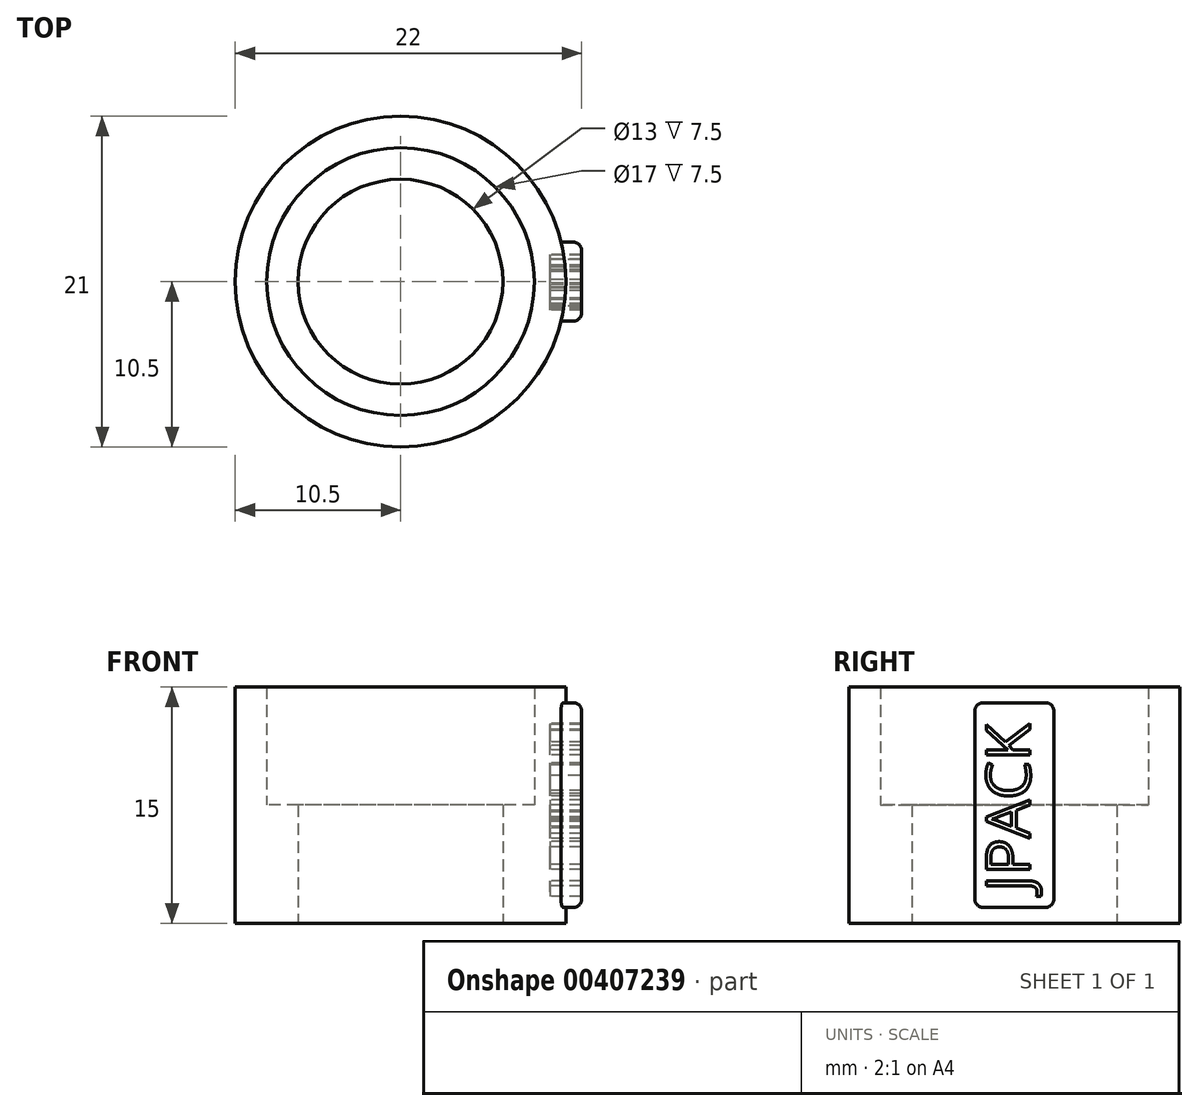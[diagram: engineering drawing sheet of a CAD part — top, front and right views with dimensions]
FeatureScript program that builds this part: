
annotation { "Feature Type Name" : "Feature", "Feature Type Description" : "" }
export const myFeature = defineFeature(function(context is Context, id is Id, definition is map)
    precondition{}
    {
        {
            var Q0;
            Q0=qCreatedBy(makeId("Top.planeOp"),FACE);
            var sketch = newSketch(context, id + "F0", { "sketchPlane" : qUnion([Q0])});
            skLineSegment(sketch, "E0", {"start": v(0, 0) * mm, "end": v(10.5, 0) * mm, "construction": true});
            skLineSegment(sketch, "E1", {"start": v(0, 0) * mm, "end": v(6.5, 0) * mm, "construction": true});
            skCircle(sketch, "E2", {"center": v(0, 0) * mm, "radius": 10.5 * mm});
            skCircle(sketch, "E3", {"center": v(0, 0) * mm, "radius": 6.5 * mm});
            skSolve(sketch);
        }
        {
            var Q0;
            Q0=makeQuery(id+"F0.imprint","IMPRINT",FACE,{"disambiguationData":[TD([[makeQuery(id+"F0.imprint","IMPRINT",EDGE,{"derivedFrom":sQuery(id+"F0.wireOp",EDGE,"E2")}),1.0]])]});
            cPlane(context, id + "F1", {"entities" : qUnion([Q0]), "cplaneType" : CPlaneType.OFFSET, "offset" : 5.5 * mm, "width" : 150 * mm, "height" : 150 * mm});
        }
        {
            var Q0;
            Q0=qCreatedBy(id+"F1.planeOp",FACE);
            cPlane(context, id + "F2", {"entities" : qUnion([Q0]), "cplaneType" : CPlaneType.OFFSET, "offset" : 2 * mm, "width" : 150 * mm, "height" : 150 * mm});
        }
        {
            var Q0;
            Q0=qCreatedBy(id+"F1.planeOp",FACE);
            var sketch = newSketch(context, id + "F3", { "sketchPlane" : qUnion([Q0])});
            skLineSegment(sketch, "E4", {"start": v(0, 0) * mm, "end": v(10.5, 0) * mm, "construction": true});
            skCircle(sketch, "E5", {"center": v(0, 0) * mm, "radius": 10.5 * mm});
            skSolve(sketch);
        }
        {
            var Q0;
            Q0 = qSketchRegion(id + "F3", true);
            extrude(context, id + "F4", {"entities" : qUnion([Q0]), "depth" : 2 * mm});
        }
        {
            var Q0;
            Q0 = qSketchRegion(id + "F0", true);
            extrude(context, id + "F5", {"entities" : qUnion([Q0]), "operationType" : NewBodyOperationType.ADD, "depth" : 5.5 * mm});
        }
        {
            var Q0;
            Q0=qCreatedBy(id+"F2.planeOp",FACE);
            var sketch = newSketch(context, id + "F6", { "sketchPlane" : qUnion([Q0])});
            skLineSegment(sketch, "E6", {"start": v(0, 0) * mm, "end": v(8.5, 0) * mm, "construction": true});
            skLineSegment(sketch, "E7", {"start": v(0, 0) * mm, "end": v(10.5, 0) * mm, "construction": true});
            skCircle(sketch, "E8", {"center": v(0, 0) * mm, "radius": 8.5 * mm});
            skCircle(sketch, "E9", {"center": v(0, 0) * mm, "radius": 10.5 * mm});
            skSolve(sketch);
        }
        {
            var Q0;
            Q0 = qSketchRegion(id + "F6", true);
            extrude(context, id + "F7", {"entities" : qUnion([Q0]), "operationType" : NewBodyOperationType.ADD, "depth" : 7.5 * mm});
        }
        {
            var Q0;
            Q0=qCreatedBy(makeId("Right.planeOp"),FACE);
            cPlane(context, id + "F8", {"entities" : qUnion([Q0]), "cplaneType" : CPlaneType.OFFSET, "offset" : 9.5 * mm, "width" : 150 * mm, "height" : 150 * mm});
        }
        {
            var Q0;
            Q0=qCreatedBy(id+"F8.planeOp",FACE);
            var sketch = newSketch(context, id + "F9", { "sketchPlane" : qUnion([Q0])});
            skLineSegment(sketch, "E10", {"start": v(0, 1) * mm, "end": v(0, 14) * mm, "construction": true});
            skLineSegment(sketch, "E11", {"start": v(0, 1) * mm, "end": v(0, 0) * mm, "construction": true});
            skLineSegment(sketch, "E12", {"start": v(0, 1) * mm, "end": v(2.5, 1) * mm});
            skLineSegment(sketch, "E13", {"start": v(2.5, 1) * mm, "end": v(2.5, 14) * mm});
            skLineSegment(sketch, "E14", {"start": v(2.5, 14) * mm, "end": v(0, 14) * mm});
            skLineSegment(sketch, "E15", {"start": v(0, 1) * mm, "end": v(-2.5, 1) * mm});
            skLineSegment(sketch, "E16", {"start": v(-2.5, 1) * mm, "end": v(-2.5, 14) * mm});
            skLineSegment(sketch, "E17", {"start": v(-2.5, 14) * mm, "end": v(0, 14) * mm});
            skSolve(sketch);
        }
        {
            var Q0;
            Q0 = qSketchRegion(id + "F9", true);
            extrude(context, id + "F10", {"entities" : qUnion([Q0]), "operationType" : NewBodyOperationType.ADD, "depth" : 2 * mm});
        }
        {
            var Q0;
            Q0=makeQuery(id+"F10.opExtrude","CAP_EDGE",EDGE,{"disambiguationData":[OSD([sQuery(id+"F9.wireOp",EDGE,"E14"),sQuery(id+"F9.wireOp",EDGE,"E17")])],"isStart":false});
            var Q1;
            Q1=makeQuery(id+"F10.opExtrude","CAP_EDGE",EDGE,{"disambiguationData":[OSD([sQuery(id+"F9.wireOp",EDGE,"E13")])],"isStart":false});
            var Q2;
            Q2=makeQuery(id+"F10.opExtrude","CAP_EDGE",EDGE,{"disambiguationData":[OSD([sQuery(id+"F9.wireOp",EDGE,"E12"),sQuery(id+"F9.wireOp",EDGE,"E15")])],"isStart":false});
            var Q3;
            Q3=makeQuery(id+"F10.opExtrude","CAP_EDGE",EDGE,{"disambiguationData":[OSD([sQuery(id+"F9.wireOp",EDGE,"E16")])],"isStart":false});
            var Q4;
            Q4=makeQuery(id+"F10.opExtrude","SWEPT_EDGE",EDGE,{"disambiguationData":[OSD([sQuery(id+"F9.wireOp",EDGE,"E13"),sQuery(id+"F9.wireOp",EDGE,"E14")])]});
            var Q5;
            Q5=makeQuery(id+"F10.opExtrude","SWEPT_EDGE",EDGE,{"disambiguationData":[OSD([sQuery(id+"F9.wireOp",EDGE,"E12"),sQuery(id+"F9.wireOp",EDGE,"E13")])]});
            var Q6;
            Q6=makeQuery(id+"F10.opExtrude","SWEPT_EDGE",EDGE,{"disambiguationData":[OSD([sQuery(id+"F9.wireOp",EDGE,"E16"),sQuery(id+"F9.wireOp",EDGE,"E17")])]});
            var Q7;
            Q7=makeQuery(id+"F10.opExtrude","SWEPT_EDGE",EDGE,{"disambiguationData":[OSD([sQuery(id+"F9.wireOp",EDGE,"E15"),sQuery(id+"F9.wireOp",EDGE,"E16")])]});
            fillet(context, id + "F11", {"entities" : qUnion([Q0, Q1, Q2, Q3, Q4, Q5, Q6, Q7]), "radius" : 0.5 * mm, "tangentPropagation" : true, "allowEdgeOverflow" : false});
        }
        {
            var Q0;
            Q0=qCreatedBy(id+"F8.planeOp",FACE);
            var sketch = newSketch(context, id + "F12", { "sketchPlane" : qUnion([Q0])});
            skLineSegment(sketch, "E18", {"start": v(0, 0) * mm, "end": v(0, 2) * mm, "construction": true});
            skLineSegment(sketch, "E19", {"start": v(0, 2) * mm, "end": v(-1.8, 2) * mm, "construction": true});
            skLineSegment(sketch, "E20", {"start": v(0, 2) * mm, "end": v(1, 2) * mm, "construction": true});
            skText(sketch, "E21", { "text": "JPACK", "fontName": "OpenSans-Regular.ttf"});
            const initialGuessF12  = {"E21": [0.001, 0.002, 0, 1, 0.0028]};
            skSetInitialGuess(sketch, initialGuessF12);
            skSolve(sketch);
        }
        {
            var Q0;
            Q0 = qSketchRegion(id + "F12", true);
            extrude(context, id + "F13", {"entities" : qUnion([Q0]), "operationType" : NewBodyOperationType.REMOVE, "depth" : 5 * mm});
        }
        {
            var Q0;
            Q0=makeQuery(id+"F4.opExtrude","CAP_FACE",FACE,{"disambiguationData":[OSD([sQuery(id+"F3.wireOp",EDGE,"E5")])],"isStart":true});
            extrude(context, id + "F14", {"entities" : qUnion([Q0]), "operationType" : NewBodyOperationType.REMOVE, "oppositeDirection" : true, "depth" : 25 * mm});
        }
    });
